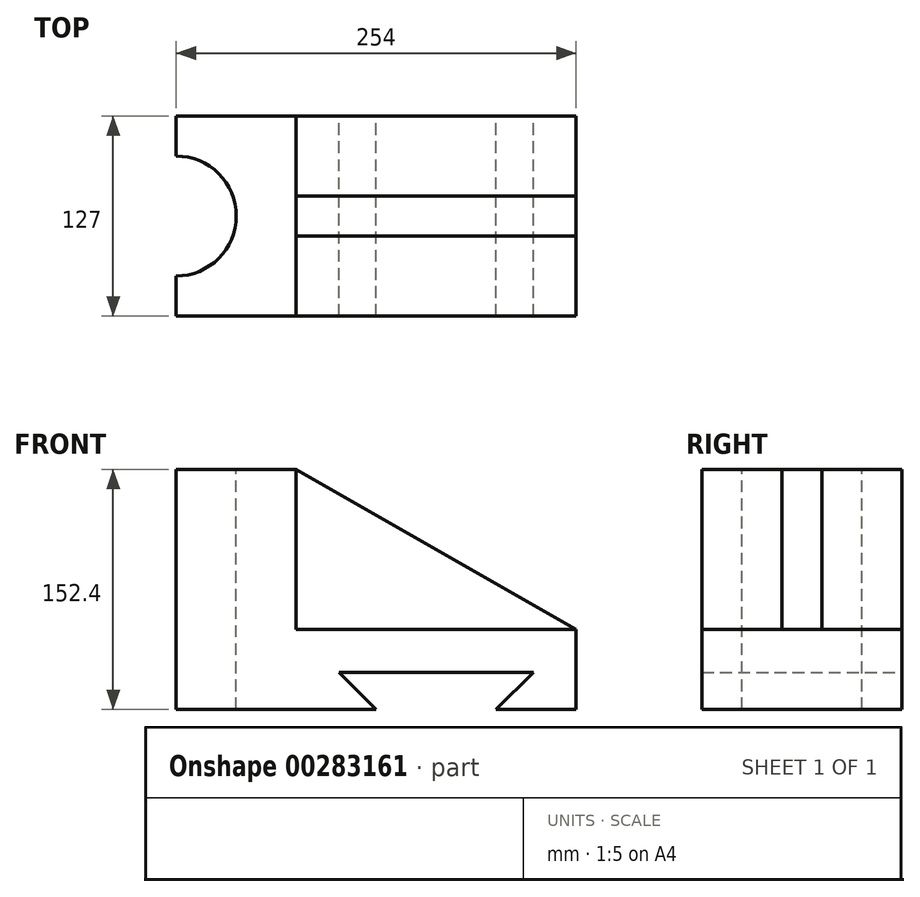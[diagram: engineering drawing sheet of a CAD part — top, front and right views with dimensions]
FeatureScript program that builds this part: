
annotation { "Feature Type Name" : "Feature", "Feature Type Description" : "" }
export const myFeature = defineFeature(function(context is Context, id is Id, definition is map)
    precondition{}
    {
        {
            var Q0;
            Q0=qCreatedBy(makeId("Front.planeOp"),FACE);
            var sketch = newSketch(context, id + "F0", { "sketchPlane" : qUnion([Q0])});
            skLineSegment(sketch, "E0", {"start": v(-31.73, 86.56) * mm, "end": v(146.07, -15.04) * mm});
            skLineSegment(sketch, "E1", {"start": v(146.07, -15.04) * mm, "end": v(146.07, -65.84) * mm});
            skLineSegment(sketch, "E2", {"start": v(-107.93, -65.84) * mm, "end": v(-107.93, 86.56) * mm});
            skLineSegment(sketch, "E3", {"start": v(-107.93, 86.56) * mm, "end": v(-31.73, 86.56) * mm});
            skLineSegment(sketch, "E4", {"start": v(146.07, -15.04) * mm, "end": v(-107.93, -15.04) * mm});
            skLineSegment(sketch, "E5", {"start": v(-31.73, 86.56) * mm, "end": v(-31.73, -15.04) * mm});
            skLineSegment(sketch, "E6", {"start": v(-107.93, -65.84) * mm, "end": v(19.07, -65.84) * mm});
            skLineSegment(sketch, "E7", {"start": v(19.07, -65.84) * mm, "end": v(-4.6, -42.17) * mm});
            skLineSegment(sketch, "E8", {"start": v(-4.6, -42.17) * mm, "end": v(118.94, -42.17) * mm});
            skLineSegment(sketch, "E9", {"start": v(118.94, -42.17) * mm, "end": v(95.27, -65.84) * mm});
            skLineSegment(sketch, "E10", {"start": v(95.27, -65.84) * mm, "end": v(146.07, -65.84) * mm});
            skSolve(sketch);
        }
        {
            var Q0;
            {var subQ0=sQuery(id+"F0.wireOp",EDGE,"E0");Q0=makeQuery(id+"F0.imprint","IMPRINT",FACE,{"disambiguationData":[TD([[makeQuery(id+"F0.imprint","IMPRINT",EDGE,{"derivedFrom":subQ0}),-1.0]])]});}
            extrude(context, id + "F1", {"entities" : qUnion([Q0]), "endBound" : BoundingType.SYMMETRIC, "depth" : 25.4 * mm});
        }
        {
            var Q0;
            {var subQ0=sQuery(id+"F0.wireOp",EDGE,"E3");Q0=makeQuery(id+"F0.imprint","IMPRINT",FACE,{"disambiguationData":[TD([[makeQuery(id+"F0.imprint","IMPRINT",EDGE,{"derivedFrom":subQ0}),-1.0]])]});}
            var Q1;
            {var subQ4=sQuery(id+"F0.wireOp",EDGE,"E1");Q1=makeQuery(id+"F0.imprint","IMPRINT",FACE,{"disambiguationData":[TD([[makeQuery(id+"F0.imprint","IMPRINT",EDGE,{"derivedFrom":subQ4}),-1.0]])]});}
            extrude(context, id + "F2", {"entities" : qUnion([Q0, Q1]), "operationType" : NewBodyOperationType.ADD, "endBound" : BoundingType.SYMMETRIC, "depth" : 127 * mm});
        }
        {
            var Q0;
            Q0=makeQuery(id+"F2.opExtrude","SWEPT_FACE",FACE,{"disambiguationData":[OSD([sQuery(id+"F0.wireOp",EDGE,"E3")])]});
            var sketch = newSketch(context, id + "F3", { "sketchPlane" : qUnion([Q0])});
            skArc(sketch, "E11", {"start": v(-107.93, 38.1) * mm, "mid": v(-69.83, 0) * mm, "end": v(-107.93, -38.1) * mm});
            skSolve(sketch);
        }
        {
            var Q0;
            Q0=sQuery(id+"F3.wireOp",VERTEX,"E11.center");
            var Q1;
            Q1=makeQuery(id+"F1.opExtrude","SWEPT_BODY",BODY,{"disambiguationData":[OSD([sQuery(id+"F0.wireOp",EDGE,"E0"),sQuery(id+"F0.wireOp",EDGE,"E4"),sQuery(id+"F0.wireOp",EDGE,"E5")])]});
            hole(context, id + "F4", {"style" : HoleStyle.SIMPLE, "endStyle" : HoleEndStyle.THROUGH, "holeDiameter" : 76.2 * mm, "tappedDepth" : 12.7 * mm, "tapClearance" : 3, "locations" : qUnion([Q0]), "scope" : qUnion([Q1])});
        }
    });
